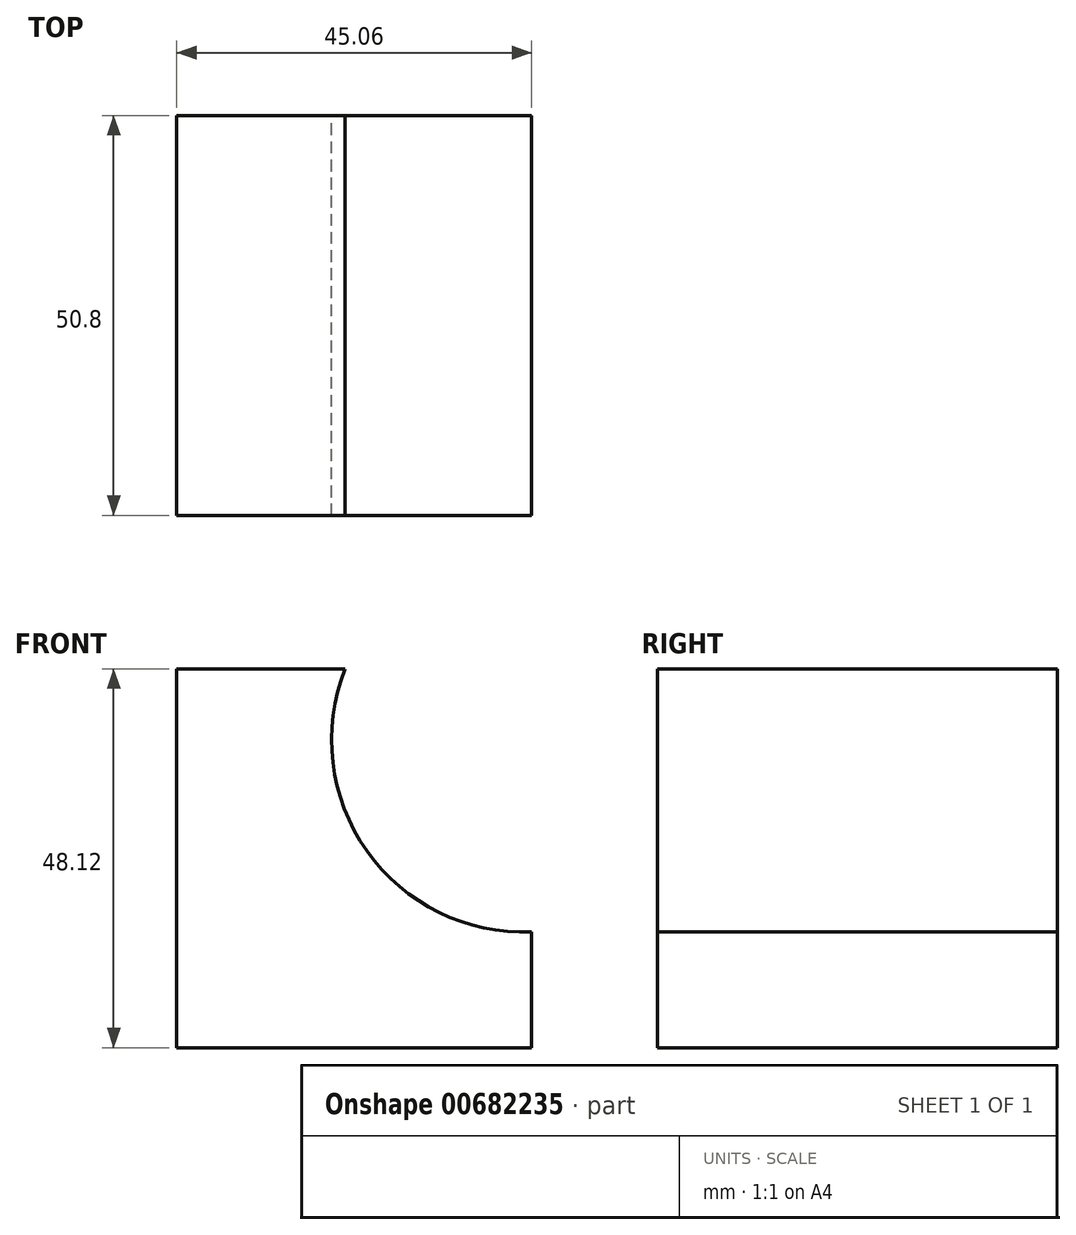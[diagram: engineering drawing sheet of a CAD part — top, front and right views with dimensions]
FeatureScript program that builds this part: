
annotation { "Feature Type Name" : "Feature", "Feature Type Description" : "" }
export const myFeature = defineFeature(function(context is Context, id is Id, definition is map)
    precondition{}
    {
        {
            var Q0;
            Q0=qCreatedBy(makeId("Front.planeOp"),FACE);
            var sketch = newSketch(context, id + "F0", { "sketchPlane" : qUnion([Q0])});
            skLineSegment(sketch, "E0", {"start": v(-69.8, 49.74) * mm, "end": v(-69.8, 1.62) * mm});
            skLineSegment(sketch, "E1", {"start": v(-69.8, 49.74) * mm, "end": v(-48.4, 49.74) * mm});
            skLineSegment(sketch, "E2", {"start": v(-69.8, 1.62) * mm, "end": v(-24.73, 1.62) * mm});
            skLineSegment(sketch, "E3", {"start": v(-24.73, 1.62) * mm, "end": v(-24.73, 16.33) * mm});
            skArc(sketch, "E4", {"start": v(-48.4, 49.74) * mm, "mid": v(-45.64, 26.6) * mm, "end": v(-24.73, 16.33) * mm});
            skSolve(sketch);
        }
        {
            var Q0;
            Q0 = qSketchRegion(id + "F0", true);
            extrude(context, id + "F1", {"entities" : qUnion([Q0]), "depth" : 50.8 * mm, "offsetDistance" : 25.4 * mm});
        }
    });
